# Revit family: Furniture-Shelf-KOHLER-Maxi_Space-K-77217T_1
name_source: partatom
category: Casework
units: mm (PartAtom-declared; Revit-internal decimal feet)

## family parameters
Cut with Voids When Loaded = No
Host = Face
OmniClass Number = 23.25.53.11.13.11
OmniClass Title = Medicine Cabinet
Room Calculation Point = No
Shared = No

## types (1)
- NA-Black
    ADA Compliant = No
    Assembly Code = E2010.30
    Construction Type = Wall Mount
    Date Modified = 08/05/2022
    Default Elevation = 60"
    Depth = 5 1/8"
    Description = New Urbanity Vertical Open Shelf
    Finish = Kohler-Metal-NA-Black
    Hardware Included = No
    Height = 29 15/16"
    Manufacturer = Kohler Co.
    Master Format 2014 = 12 35 30.23
    Master Format 2014 Name = Bathroom Casework
    Material = Aluminium
    Model = K-77217T-NA
    Product Finish = Kohler-Metal-NA-Black
    Product Name = Maxi Space
    Type = 1
    URL = http://www.kohler.com.cn
    WaterSense Certified = No
    Width = 11 13/16"

## geometry (parser evidence)
native form markers: Sweep x5
no freeform markers — native parametric forms only
